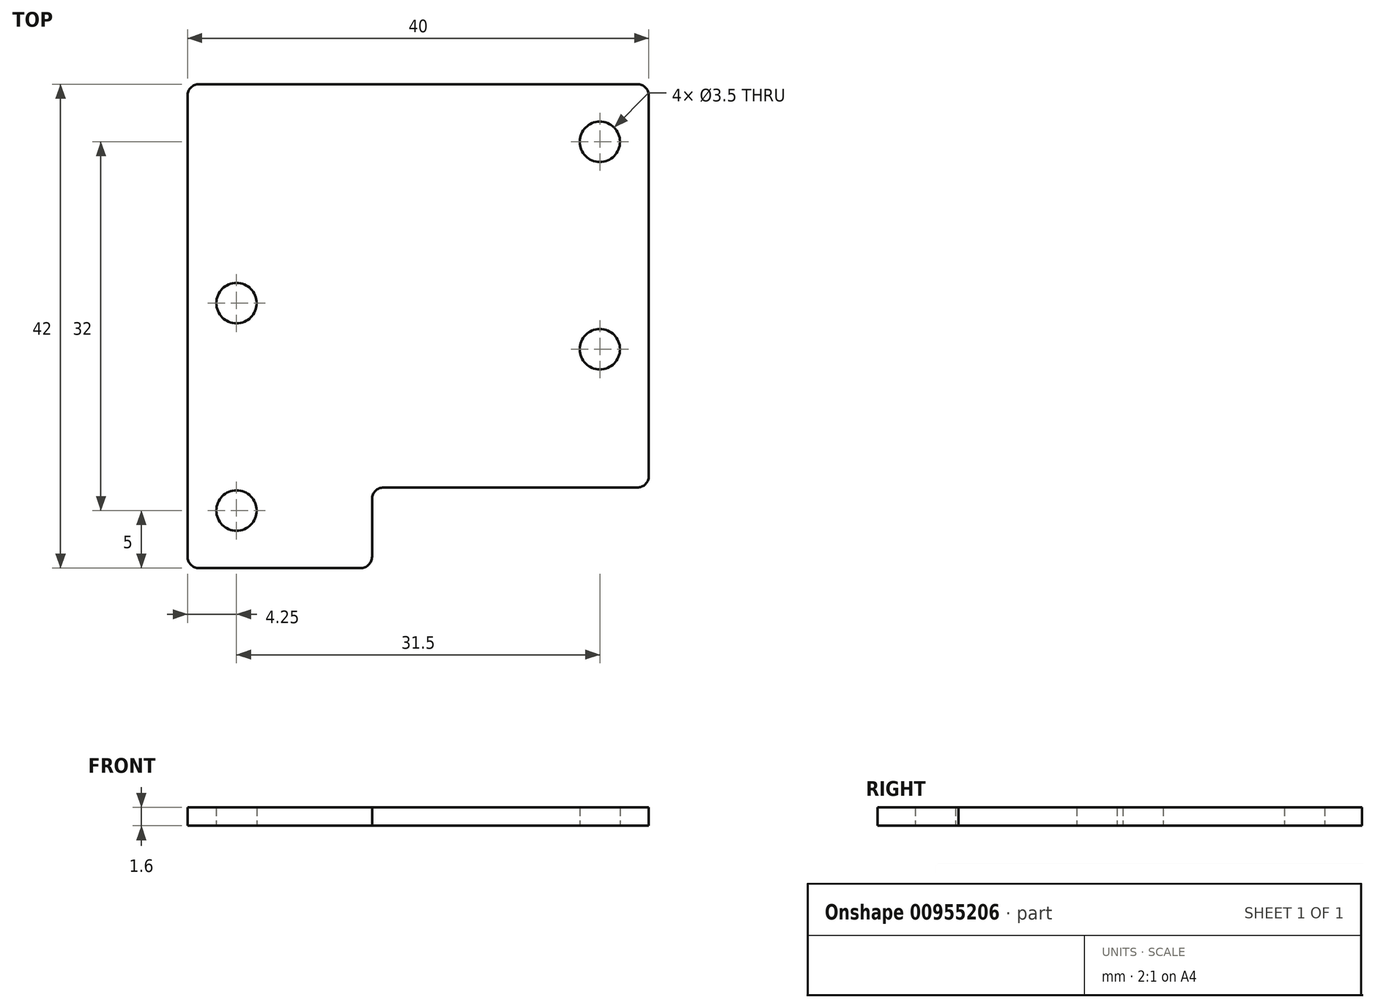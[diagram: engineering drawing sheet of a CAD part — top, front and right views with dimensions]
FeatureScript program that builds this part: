
annotation { "Feature Type Name" : "Feature", "Feature Type Description" : "" }
export const myFeature = defineFeature(function(context is Context, id is Id, definition is map)
    precondition{}
    {
        {
            var Q0;
            Q0=qCreatedBy(makeId("Top.planeOp"),FACE);
            var sketch = newSketch(context, id + "F0", { "sketchPlane" : qUnion([Q0])});
            skCircle(sketch, "E0", {"center": v(15.75, -2) * mm, "radius": 1.75 * mm});
            skCircle(sketch, "E1", {"center": v(15.75, 16) * mm, "radius": 1.75 * mm});
            skLineSegment(sketch, "E2", {"start": v(15.75, -2) * mm, "end": v(15.75, 16) * mm, "construction": true});
            skLineSegment(sketch, "E3", {"start": v(15.75, 7) * mm, "end": v(-4.25, 7) * mm, "construction": true});
            skLineSegment(sketch, "E4", {"start": v(-4.25, 1) * mm, "end": v(-4.25, 13) * mm, "construction": true});
            skLineSegment(sketch, "E5", {"start": v(-4.25, 13) * mm, "end": v(15.75, 13) * mm, "construction": true});
            skLineSegment(sketch, "E6", {"start": v(-4.25, 1) * mm, "end": v(15.75, 1) * mm, "construction": true});
            skCircle(sketch, "E7", {"center": v(15.75, -2) * mm, "radius": 4.25 * mm, "construction": true});
            skCircle(sketch, "E8", {"center": v(15.75, 16) * mm, "radius": 4.25 * mm, "construction": true});
            skLineSegment(sketch, "E9", {"start": v(15.75, 16) * mm, "end": v(20, 16) * mm, "construction": true});
            skLineSegment(sketch, "E10", {"start": v(20, 16) * mm, "end": v(20, -2) * mm, "construction": true});
            skLineSegment(sketch, "E11", {"start": v(15.75, 16) * mm, "end": v(11.5, 16) * mm, "construction": true});
            skLineSegment(sketch, "E12", {"start": v(11.5, 16) * mm, "end": v(11.5, -2) * mm, "construction": true});
            skLineSegment(sketch, "E13", {"start": v(11.5, -2) * mm, "end": v(15.75, -2) * mm, "construction": true});
            skCircle(sketch, "E14.1.0", {"center": v(-15.75, -16) * mm, "radius": 1.75 * mm});
            skCircle(sketch, "E14.1.1", {"center": v(-15.75, -16) * mm, "radius": 4.25 * mm, "construction": true});
            skLineSegment(sketch, "E14.1.2", {"start": v(-20, -16) * mm, "end": v(-20, 2) * mm, "construction": true});
            skCircle(sketch, "E14.1.3", {"center": v(-15.75, 2) * mm, "radius": 4.25 * mm, "construction": true});
            skCircle(sketch, "E14.1.4", {"center": v(-15.75, 2) * mm, "radius": 1.75 * mm});
            skLineSegment(sketch, "E14.1.5", {"start": v(-11.5, -16) * mm, "end": v(-11.5, 2) * mm, "construction": true});
            skLineSegment(sketch, "E14.1.6", {"start": v(4.25, -1) * mm, "end": v(-15.75, -1) * mm, "construction": true});
            skLineSegment(sketch, "E14.1.7", {"start": v(4.25, -13) * mm, "end": v(-15.75, -13) * mm, "construction": true});
            skLineSegment(sketch, "E14.1.8", {"start": v(4.25, -1) * mm, "end": v(4.25, -13) * mm, "construction": true});
            skPoint(sketch, "E14.center", {"position": v(0, 0) * mm});
            skLineSegment(sketch, "E15.bottom", {"start": v(-20, 21) * mm, "end": v(20, 21) * mm});
            skLineSegment(sketch, "E15.top", {"start": v(-20, -21) * mm, "end": v(20, -21) * mm});
            skLineSegment(sketch, "E15.left", {"start": v(-20, 21) * mm, "end": v(-20, -21) * mm});
            skLineSegment(sketch, "E15.right", {"start": v(20, 21) * mm, "end": v(20, -21) * mm});
            skLineSegment(sketch, "E16", {"start": v(-4, -21) * mm, "end": v(-4, -14) * mm});
            skLineSegment(sketch, "E17", {"start": v(-4, -14) * mm, "end": v(20, -14) * mm});
            skSolve(sketch);
        }
        {
            var Q0;
            Q0=makeQuery(id+"F0.imprint","IMPRINT",FACE,{"disambiguationData":[TD([[makeQuery(id+"F0.imprint","IMPRINT",EDGE,{"derivedFrom":sQuery(id+"F0.wireOp",EDGE,"E0")}),-1.0]])]});
            extrude(context, id + "F1", {"entities" : qUnion([Q0]), "depth" : 1.6 * mm, "offsetDistance" : 25 * mm});
        }
        {
            var Q0;
            Q0=makeQuery(id+"F1.opExtrude","SWEPT_EDGE",EDGE,{"disambiguationData":[OSD([sQuery(id+"F0.wireOp",EDGE,"E15.top"),sQuery(id+"F0.wireOp",EDGE,"E15.left")])]});
            var Q1;
            Q1=makeQuery(id+"F1.opExtrude","SWEPT_EDGE",EDGE,{"disambiguationData":[OSD([sQuery(id+"F0.wireOp",EDGE,"E15.top"),sQuery(id+"F0.wireOp",EDGE,"E15.right")])]});
            var Q2;
            Q2=makeQuery(id+"F1.opExtrude","SWEPT_EDGE",EDGE,{"disambiguationData":[OSD([sQuery(id+"F0.wireOp",EDGE,"E15.bottom"),sQuery(id+"F0.wireOp",EDGE,"E15.right")])]});
            var Q3;
            Q3=makeQuery(id+"F1.opExtrude","SWEPT_EDGE",EDGE,{"disambiguationData":[OSD([sQuery(id+"F0.wireOp",EDGE,"E15.bottom"),sQuery(id+"F0.wireOp",EDGE,"E15.left")])]});
            var Q4;
            Q4=makeQuery(id+"F1.opExtrude","SWEPT_EDGE",EDGE,{"disambiguationData":[OSD([sQuery(id+"F0.wireOp",EDGE,"E16"),sQuery(id+"F0.wireOp",EDGE,"E17")])]});
            fillet(context, id + "F2", {"entities" : qUnion([Q0, Q1, Q2, Q3, Q4]), "radius" : 1 * mm, "tangentPropagation" : true, "allowEdgeOverflow" : false});
        }
    });
